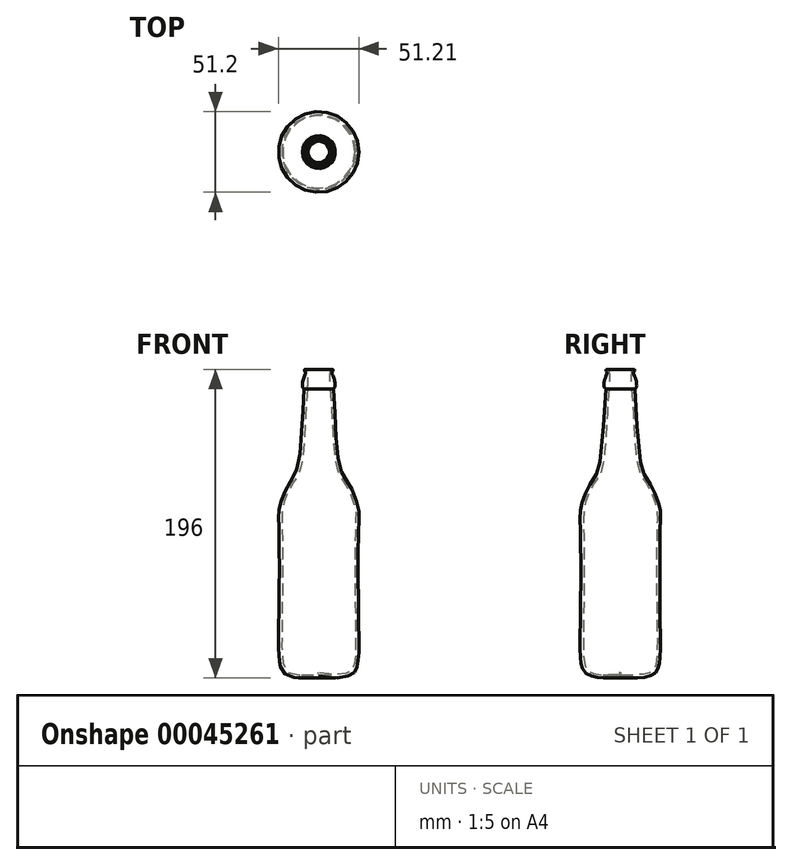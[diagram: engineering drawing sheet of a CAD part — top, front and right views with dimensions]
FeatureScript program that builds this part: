
annotation { "Feature Type Name" : "Feature", "Feature Type Description" : "" }
export const myFeature = defineFeature(function(context is Context, id is Id, definition is map)
    precondition{}
    {
        {
            var Q0;
            Q0=qCreatedBy(makeId("Front.planeOp"),FACE);
            var sketch = newSketch(context, id + "F0", { "sketchPlane" : qUnion([Q0])});
            skFitSpline(sketch, "E0", {"points": [v(-34.46, 68.35) * mm, v(-29.72, 16.86) * mm, v(-24.1, 7.19) * mm, v(-18.43, -8.26) * mm, v(-18.26, -15.53) * mm, v(-18.54, -65) * mm, v(-18.26, -99.29) * mm, v(-18.83, -105.76) * mm, v(-20.12, -110.22) * mm, v(-23.3, -113.37) * mm, v(-33.97, -115.26) * mm, v(-43.7, -114.08) * mm], "startDerivative": vector(29, -357.67) * mm, "endDerivative": vector(-185.26, -1.92) * mm});
            skFitSpline(sketch, "E1", {"points": [v(-34.46, 68.35) * mm, v(-33.81, 68.94) * mm, v(-33.36, 69.48) * mm, v(-33.27, 70.96) * mm, v(-33.8, 74.3) * mm, v(-35.31, 78.36) * mm, v(-35.04, 79.37) * mm, v(-34.6, 79.77) * mm, v(-34.53, 80.34) * mm, v(-35.54, 80.63) * mm], "startDerivative": vector(13.68, 7.15) * mm, "endDerivative": vector(-19.36, -6.47) * mm});
            skLineSegment(sketch, "E2", {"start": v(-43.7, -123.85) * mm, "end": v(-43.7, 98.5) * mm});
            skLineSegment(sketch, "E3", {"start": v(-35.54, 80.63) * mm, "end": v(-43.7, 80.63) * mm});
            skFitSpline(sketch, "E4.0", {"points": [v(-36.46, 68.19) * mm, v(-36.16, 64.48) * mm, v(-35.67, 56.88) * mm, v(-35.08, 45.53) * mm, v(-34.55, 36.61) * mm, v(-34.01, 30.1) * mm, v(-33.52, 25.6) * mm, v(-32.93, 21.55) * mm, v(-32.3, 18.6) * mm, v(-31.72, 16.5) * mm, v(-31.22, 15.08) * mm, v(-30.68, 13.81) * mm, v(-29.9, 12.29) * mm, v(-28.87, 10.65) * mm, v(-27.83, 9.23) * mm, v(-27.03, 8.1) * mm, v(-26.44, 7.21) * mm, v(-25.96, 6.42) * mm, v(-25.58, 5.74) * mm, v(-25.19, 5.02) * mm, v(-24.7, 4.04) * mm, v(-23.94, 2.36) * mm, v(-23.02, 0.1) * mm, v(-22.03, -2.67) * mm, v(-21.34, -4.89) * mm, v(-20.89, -6.52) * mm, v(-20.6, -7.65) * mm, v(-20.39, -8.65) * mm, v(-20.24, -9.5) * mm, v(-20.15, -10.25) * mm, v(-20.09, -11.17) * mm, v(-20.1, -12.12) * mm, v(-20.14, -13.27) * mm, v(-20.2, -14.27) * mm, v(-20.26, -15.45) * mm, v(-20.33, -17.28) * mm, v(-20.4, -20.01) * mm, v(-20.48, -23.9) * mm, v(-20.55, -28.31) * mm, v(-20.6, -34.77) * mm, v(-20.64, -43.67) * mm, v(-20.62, -54.93) * mm, v(-20.55, -65.97) * mm, v(-20.41, -76.05) * mm, v(-20.3, -83.49) * mm, v(-20.24, -88.74) * mm, v(-20.2, -92.3) * mm, v(-20.2, -95.46) * mm, v(-20.22, -97.72) * mm, v(-20.25, -99.3) * mm, v(-20.3, -100.7) * mm, v(-20.39, -102.2) * mm, v(-20.54, -103.71) * mm, v(-20.73, -105.08) * mm, v(-21, -106.47) * mm, v(-21.32, -107.78) * mm, v(-21.66, -108.76) * mm, v(-21.96, -109.45) * mm, v(-22.29, -110.03) * mm, v(-22.64, -110.5) * mm, v(-23.1, -110.92) * mm, v(-23.55, -111.24) * mm, v(-24.11, -111.55) * mm, v(-24.83, -111.87) * mm, v(-25.69, -112.18) * mm, v(-26.97, -112.55) * mm, v(-28.77, -112.94) * mm, v(-30.65, -113.18) * mm, v(-32.1, -113.27) * mm, v(-32.96, -113.29) * mm, v(-33.61, -113.27) * mm, v(-34.23, -113.24) * mm, v(-34.95, -113.17) * mm, v(-35.81, -113.04) * mm, v(-36.98, -112.82) * mm, v(-38.56, -112.5) * mm, v(-40.83, -112.16) * mm, v(-42.68, -112.07) * mm, v(-43.72, -112.08) * mm]});
            skFitSpline(sketch, "E5", {"points": [v(-36.46, 68.19) * mm, v(-36.9, 73.1) * mm, v(-36.46, 80.63) * mm], "startDerivative": vector(-1.4, 10.4) * mm, "endDerivative": vector(1.31, 14.36) * mm});
            skSolve(sketch);
        }
        {
            var Q0;
            {var subQ4=sQuery(id+"F0.wireOp",EDGE,"E0");Q0=makeQuery(id+"F0.imprint","IMPRINT",FACE,{"disambiguationData":[TD([[makeQuery(id+"F0.imprint","IMPRINT",EDGE,{"derivedFrom":subQ4}),-1.0]])]});}
            var Q1;
            Q1=sQuery(id+"F0.wireOp",EDGE,"E2");
            revolve(context, id + "F1", {"entities" : qUnion([Q0]), "axis" : qUnion([Q1]), "revolveType" : RevolveType.FULL});
        }
    });
